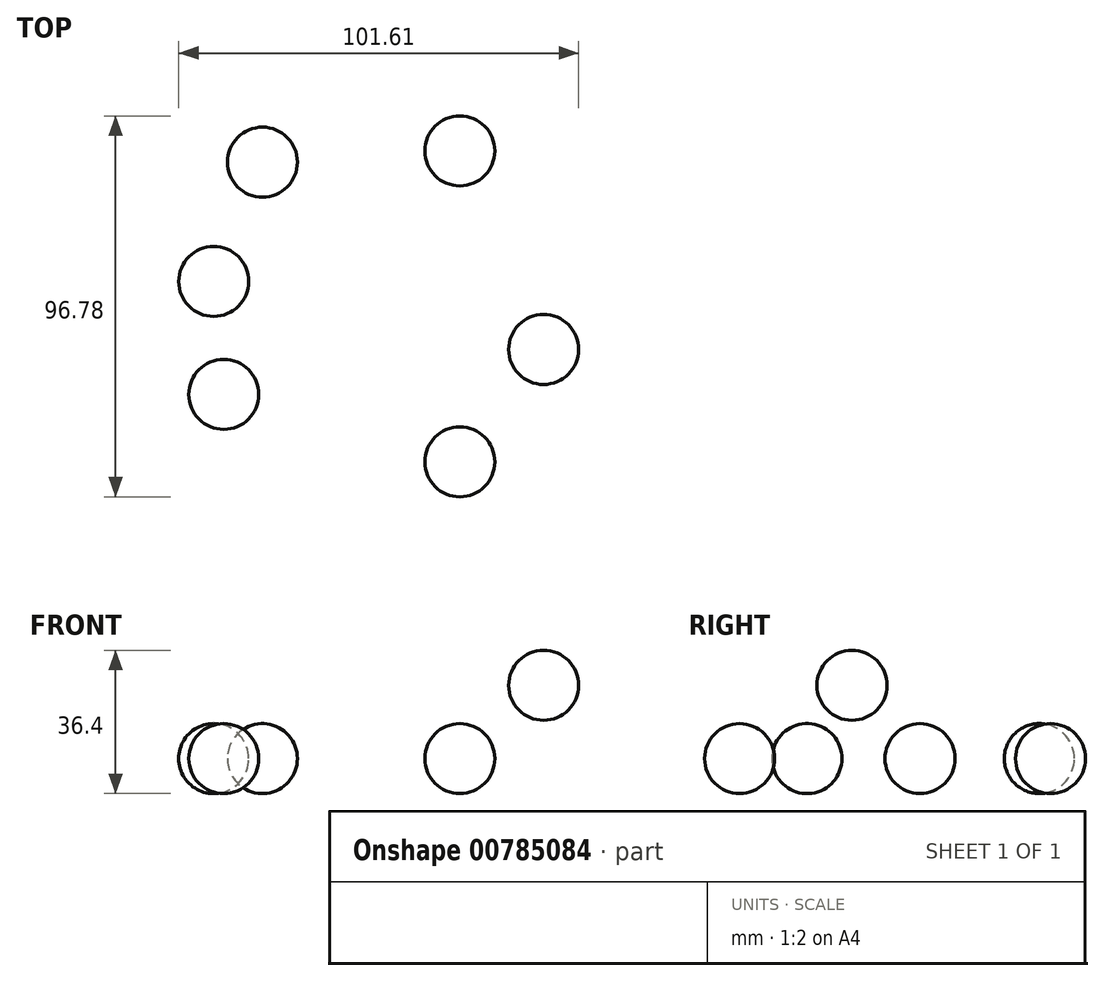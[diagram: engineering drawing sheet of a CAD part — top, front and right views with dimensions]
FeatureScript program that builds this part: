
annotation { "Feature Type Name" : "Feature", "Feature Type Description" : "" }
export const myFeature = defineFeature(function(context is Context, id is Id, definition is map)
    precondition{}
    {
        {
            var Q0;
            Q0=qCreatedBy(makeId("Front.planeOp"),FACE);
            var sketch = newSketch(context, id + "F0", { "sketchPlane" : qUnion([Q0])});
            skArc(sketch, "E0", {"start": v(21.3, 27.5) * mm, "mid": v(12.4, 18.62) * mm, "end": v(21.3, 9.73) * mm});
            skLineSegment(sketch, "E1", {"start": v(21.3, 18.62) * mm, "end": v(21.3, 31.85) * mm});
            skLineSegment(sketch, "E2", {"start": v(21.3, 31.85) * mm, "end": v(21.3, 2.54) * mm});
            skSolve(sketch);
        }
        {
            var Q0;
            Q0 = qSketchRegion(id + "F0", true);
            var Q1;
            Q1=sQuery(id+"F0.wireOp",EDGE,"E2");
            revolve(context, id + "F1", {"surfaceOperationType" : NewSurfaceOperationType.NEW, "entities" : qUnion([Q0]), "axis" : qUnion([Q1]), "revolveType" : RevolveType.FULL});
        }
        {
            var Q0;
            Q0=qCreatedBy(makeId("Top.planeOp"),FACE);
            var sketch = newSketch(context, id + "F2", { "sketchPlane" : qUnion([Q0])});
            skArc(sketch, "E3", {"start": v(-50.15, 38.7) * mm, "mid": v(-41.26, 47.6) * mm, "end": v(-50.15, 56.49) * mm});
            skLineSegment(sketch, "E4", {"start": v(-50.15, 47.6) * mm, "end": v(-50.15, 38.7) * mm});
            skLineSegment(sketch, "E5", {"start": v(-50.15, 38.7) * mm, "end": v(-50.15, 56.49) * mm});
            skSolve(sketch);
        }
        {
            var Q0;
            Q0 = qSketchRegion(id + "F2", true);
            var Q1;
            Q1=sQuery(id+"F2.wireOp",EDGE,"E5");
            revolve(context, id + "F3", {"surfaceOperationType" : NewSurfaceOperationType.NEW, "entities" : qUnion([Q0]), "axis" : qUnion([Q1]), "revolveType" : RevolveType.FULL});
        }
        {
            var Q0;
            Q0=qCreatedBy(makeId("Top.planeOp"),FACE);
            var sketch = newSketch(context, id + "F4", { "sketchPlane" : qUnion([Q0])});
            skArc(sketch, "E6", {"start": v(-62.54, 8.4) * mm, "mid": v(-53.65, 17.28) * mm, "end": v(-62.54, 26.17) * mm});
            skLineSegment(sketch, "E7", {"start": v(-62.54, 17.28) * mm, "end": v(-62.54, 8.4) * mm});
            skLineSegment(sketch, "E8", {"start": v(-62.54, 8.4) * mm, "end": v(-62.54, 26.17) * mm});
            skSolve(sketch);
        }
        {
            var Q0;
            Q0 = qSketchRegion(id + "F4", true);
            var Q1;
            Q1=sQuery(id+"F4.wireOp",EDGE,"E7");
            revolve(context, id + "F5", {"surfaceOperationType" : NewSurfaceOperationType.NEW, "entities" : qUnion([Q0]), "axis" : qUnion([Q1]), "revolveType" : RevolveType.FULL});
        }
        {
            var Q0;
            Q0=qCreatedBy(makeId("Top.planeOp"),FACE);
            var sketch = newSketch(context, id + "F6", { "sketchPlane" : qUnion([Q0])});
            skArc(sketch, "E9", {"start": v(-59.98, -20.32) * mm, "mid": v(-51.09, -11.43) * mm, "end": v(-59.98, -2.54) * mm});
            skLineSegment(sketch, "E10", {"start": v(-59.98, -11.43) * mm, "end": v(-59.98, -20.32) * mm});
            skLineSegment(sketch, "E11", {"start": v(-59.98, -20.32) * mm, "end": v(-59.98, -2.54) * mm});
            skSolve(sketch);
        }
        {
            var Q0;
            Q0 = qSketchRegion(id + "F6", true);
            var Q1;
            Q1=sQuery(id+"F6.wireOp",EDGE,"E11");
            revolve(context, id + "F7", {"surfaceOperationType" : NewSurfaceOperationType.NEW, "entities" : qUnion([Q0]), "axis" : qUnion([Q1]), "revolveType" : RevolveType.FULL});
        }
        {
            var Q0;
            Q0=qCreatedBy(makeId("Top.planeOp"),FACE);
            var sketch = newSketch(context, id + "F8", { "sketchPlane" : qUnion([Q0])});
            skArc(sketch, "E12", {"start": v(0, 41.56) * mm, "mid": v(8.9, 50.45) * mm, "end": v(0, 59.34) * mm});
            skLineSegment(sketch, "E13", {"start": v(0, 59.34) * mm, "end": v(0, 41.56) * mm});
            skSolve(sketch);
        }
        {
            var Q0;
            Q0 = qSketchRegion(id + "F8", true);
            var Q1;
            Q1=sQuery(id+"F8.wireOp",EDGE,"E13");
            revolve(context, id + "F9", {"surfaceOperationType" : NewSurfaceOperationType.NEW, "entities" : qUnion([Q0]), "axis" : qUnion([Q1]), "revolveType" : RevolveType.FULL});
        }
        {
            var Q0;
            Q0=qCreatedBy(makeId("Top.planeOp"),FACE);
            var sketch = newSketch(context, id + "F10", { "sketchPlane" : qUnion([Q0])});
            skArc(sketch, "E14", {"start": v(0, -37.44) * mm, "mid": v(8.9, -28.55) * mm, "end": v(0, -19.66) * mm});
            skLineSegment(sketch, "E15", {"start": v(0, -19.66) * mm, "end": v(0, -37.44) * mm});
            skSolve(sketch);
        }
        {
            var Q0;
            Q0 = qSketchRegion(id + "F10", true);
            var Q1;
            Q1=sQuery(id+"F10.wireOp",EDGE,"E15");
            revolve(context, id + "F11", {"surfaceOperationType" : NewSurfaceOperationType.NEW, "entities" : qUnion([Q0]), "axis" : qUnion([Q1]), "revolveType" : RevolveType.FULL});
        }
    });
